# Revit family: 33-76-001 DN80-400
name_source: partatom
category: Pipe Accessories
units: mm (PartAtom-declared; Revit-internal decimal feet)

## family parameters
Always vertical = No
Cut with Voids When Loaded = No
Part Type = Valve - Breaks Into
Round Connector Dimension = Use Diameter
Shared = No
Work Plane-Based = No

## types (8) — shared parameters
1 = 1 mm  [stored 0.00328084 ft]
2 = 2 mm  [stored 0.00656168 ft]
DN080_PN16 = 33-080-76-0140099
33-080-76-0140099
DN100_PN16 = 33-100-76-0140099
DN150_PN16 = 33-150-76-0140099
DN200_PN16 = 33-200-76-0140099
DN250_PN16 = 33-250-76-0140099
DN300_PN16 = 33-300-76-0140087
DN350_PN16 = 33-350-76-0140087
DN400_PN16 = 33-400-76-0140087
Description_ = AVK GATE VALVE, SOCKET ENDS, PN16
Search_table = 33-76-001 DN80-400
T1 = 16 mm  [stored 0.0524934 ft]
Thickness = 9 mm  [stored 0.0295276 ft]
URL product pages = https://www.avkvalves.com
zero-valued in all types: Bonnet_FL_T, Default Elevation, Dim4

## per-type parameters (varying)
- DN080_PN16: Body_H=210 mm; Body_dim1=78 mm; Body_dim2=45 mm; Bolt=15 mm  [stored 0.0492126 ft]; Bolt_T=9 mm  [stored 0.0295276 ft]; Bonne_end=338 mm; Bonnet_Bolt1=9 mm  [stored 0.0295276 ft]; Bonnet_Bolt2=14 mm  [stored 0.0459318 ft]; Bonnet_W=72 mm; Bonnet_dim=43 mm; Bonnet_dim1=58 mm; Bonnet_dim2=8 mm  [stored 0.0262467 ft]; Bonnet_dim3=43 mm; Bonnet_dim4=35 mm; Bonnet_dim5=28 mm  [stored 0.0918635 ft]; Bonnet_dim6=25 mm  [stored 0.082021 ft]; Bore=40 mm  [stored 0.131234 ft]; DN=80 mm; Dd=101 mm; Dim1=67 mm; Dim2=75 mm; Dim3=66 mm; Disk=47 mm  [stored 0.154199 ft]; EPDM=99 mm; F1=17 mm  [stored 0.0557743 ft]; Fillet=15 mm  [stored 0.0492126 ft]; H=84 mm; H3=375 mm; L=298 mm; Location1=262 mm; Location2=75 mm; Rib_dim1=38 mm; Rib_dim2=31 mm; W=173 mm; W_actual=87 mm
- DN100_PN16: Body_H=235 mm; Body_dim1=87 mm; Body_dim2=48 mm; Bolt=17 mm  [stored 0.0557743 ft]; Bolt_T=10 mm  [stored 0.0328084 ft]; Bonne_end=367 mm; Bonnet_Bolt1=11 mm  [stored 0.0360892 ft]; Bonnet_Bolt2=16 mm  [stored 0.0524934 ft]; Bonnet_W=81 mm; Bonnet_dim=48 mm; Bonnet_dim1=62 mm; Bonnet_dim2=9 mm  [stored 0.0295276 ft]; Bonnet_dim3=48 mm; Bonnet_dim4=37 mm; Bonnet_dim5=30 mm  [stored 0.0984252 ft]; Bonnet_dim6=27 mm  [stored 0.0885827 ft]; Bore=50 mm; DN=100 mm; Dd=121 mm; Dim1=75 mm; Dim2=84 mm; Dim3=75 mm; Disk=50 mm; EPDM=119 mm; F1=19 mm  [stored 0.062336 ft]; Fillet=18 mm  [stored 0.0590551 ft]; H=94 mm; H3=408 mm; L=317 mm; Location1=279 mm; Location2=79 mm; Rib_dim1=43 mm; Rib_dim2=34 mm; W=194 mm; W_actual=97 mm
- DN150_PN16: Body_H=303 mm; Body_dim1=123 mm; Body_dim2=53 mm; Bolt=17 mm  [stored 0.0557743 ft]; Bolt_T=10 mm  [stored 0.0328084 ft]; Bonne_end=477 mm; Bonnet_Bolt1=12 mm  [stored 0.0393701 ft]; Bonnet_Bolt2=18 mm  [stored 0.0590551 ft]; Bonnet_W=114 mm; Bonnet_dim=48 mm; Bonnet_dim1=68 mm; Bonnet_dim2=10 mm  [stored 0.0328084 ft]; Bonnet_dim3=48 mm; Bonnet_dim4=41 mm; Bonnet_dim5=33 mm; Bonnet_dim6=30 mm  [stored 0.0984252 ft]; Bore=75 mm; DN=150 mm; Dd=173 mm; Dim1=97 mm; Dim2=110 mm; Dim3=100 mm; Disk=55 mm; EPDM=171 mm; F1=19 mm  [stored 0.062336 ft]; Fillet=20 mm  [stored 0.0656168 ft]; H=121 mm; H3=530 mm; L=351 mm; Location1=309 mm; Location2=88 mm; Rib_dim1=61 mm; Rib_dim2=49 mm; W=274 mm; W_actual=137 mm
- DN200_PN16: Body_H=368 mm; Body_dim1=150 mm; Body_dim2=58 mm; Bolt=22 mm  [stored 0.0721785 ft]; Bolt_T=12 mm  [stored 0.0393701 ft]; Bonne_end=581 mm; Bonnet_Bolt1=13 mm  [stored 0.0426509 ft]; Bonnet_Bolt2=20 mm  [stored 0.0656168 ft]; Bonnet_W=139 mm; Bonnet_dim=60 mm; Bonnet_dim1=75 mm; Bonnet_dim2=11 mm  [stored 0.0360892 ft]; Bonnet_dim3=60 mm; Bonnet_dim4=45 mm; Bonnet_dim5=36 mm; Bonnet_dim6=33 mm; Bore=100 mm; DN=200 mm; Dd=225 mm; Dim1=110 mm; Dim2=140 mm; Dim3=125 mm; Disk=60 mm; EPDM=223 mm; F1=24 mm  [stored 0.0787402 ft]; Fillet=22 mm  [stored 0.0721785 ft]; H=147 mm; H3=646 mm; L=387 mm; Location1=341 mm; Location2=97 mm; Rib_dim1=74 mm; Rib_dim2=59 mm; W=334 mm; W_actual=167 mm
- DN250_PN16: Body_H=438 mm; Body_dim1=190 mm; Body_dim2=70 mm; Bolt=24 mm  [stored 0.0787402 ft]; Bolt_T=14 mm  [stored 0.0459318 ft]; Bonne_end=729 mm; Bonnet_Bolt1=14 mm  [stored 0.0459318 ft]; Bonnet_Bolt2=22 mm  [stored 0.0721785 ft]; Bonnet_W=175 mm; Bonnet_dim=68 mm; Bonnet_dim1=91 mm; Bonnet_dim2=12 mm  [stored 0.0393701 ft]; Bonnet_dim3=68 mm; Bonnet_dim4=55 mm; Bonnet_dim5=44 mm; Bonnet_dim6=39 mm  [stored 0.127953 ft]; Bore=125 mm; DN=250 mm; Dd=277 mm; Dim1=115 mm; Dim2=165 mm; Dim3=150 mm; Disk=72 mm; EPDM=275 mm; F1=27 mm  [stored 0.0885827 ft]; Fillet=24 mm  [stored 0.0787402 ft]; H=175 mm; H3=810 mm; L=428 mm; Location1=377 mm; Location2=107 mm; Rib_dim1=94 mm; Rib_dim2=75 mm; W=422 mm; W_actual=211 mm
- DN300_PN16: Body_H=525 mm; Body_dim1=203 mm; Body_dim2=69 mm; Bolt=24 mm  [stored 0.0787402 ft]; Bolt_T=14 mm  [stored 0.0459318 ft]; Bonne_end=829 mm; Bonnet_Bolt1=16 mm  [stored 0.0524934 ft]; Bonnet_Bolt2=23 mm; Bonnet_W=188 mm; Bonnet_dim=68 mm; Bonnet_dim1=89 mm; Bonnet_dim2=13 mm  [stored 0.0426509 ft]; Bonnet_dim3=68 mm; Bonnet_dim4=54 mm; Bonnet_dim5=43 mm; Bonnet_dim6=39 mm  [stored 0.127953 ft]; Bore=150 mm; DN=300 mm; Dd=329 mm; Dim1=130 mm; Dim2=195 mm; Dim3=182 mm; Disk=71 mm; EPDM=327 mm; F1=27 mm  [stored 0.0885827 ft]; Fillet=26 mm; H=210 mm; H3=921 mm; L=458 mm; Location1=403 mm; Location2=115 mm; Rib_dim1=100 mm; Rib_dim2=80 mm; W=452 mm; W_actual=226 mm
- DN350_PN16: Body_H=570 mm; Body_dim1=254 mm; Body_dim2=78 mm; Bolt=29 mm; Bolt_T=16 mm  [stored 0.0524934 ft]; Bonne_end=1037 mm; Bonnet_Bolt1=17 mm  [stored 0.0557743 ft]; Bonnet_Bolt2=25 mm  [stored 0.082021 ft]; Bonnet_W=234 mm; Bonnet_dim=185 mm; Bonnet_dim1=101 mm; Bonnet_dim2=14 mm  [stored 0.0459318 ft]; Bonnet_dim3=80 mm; Bonnet_dim4=61 mm; Bonnet_dim5=49 mm; Bonnet_dim6=44 mm; Bore=175 mm; DN=350 mm; Dd=381 mm; Dim1=108 mm; Dim2=215 mm; Dim3=205 mm; Disk=80 mm; EPDM=379 mm; F1=32 mm  [stored 0.104987 ft]; Fillet=28 mm  [stored 0.0918635 ft]; H=228 mm; H3=1152 mm; L=460 mm; Location1=405 mm; Location2=115 mm; Rib_dim1=125 mm; Rib_dim2=100 mm; W=564 mm; W_actual=282 mm
- DN400_PN16: Body_H=638 mm; Body_dim1=254 mm; Body_dim2=80 mm; Bolt=29 mm; Bolt_T=16 mm  [stored 0.0524934 ft]; Bonne_end=1088 mm; Bonnet_Bolt1=18 mm  [stored 0.0590551 ft]; Bonnet_Bolt2=27 mm  [stored 0.0885827 ft]; Bonnet_W=234 mm; Bonnet_dim=165 mm; Bonnet_dim1=104 mm; Bonnet_dim2=15 mm  [stored 0.0492126 ft]; Bonnet_dim3=80 mm; Bonnet_dim4=62 mm; Bonnet_dim5=50 mm; Bonnet_dim6=45 mm; Bore=200 mm; DN=400 mm; Dd=432 mm; Dim1=110 mm; Dim2=240 mm; Dim3=230 mm; Disk=82 mm; EPDM=430 mm; F1=32 mm  [stored 0.104987 ft]; Fillet=30 mm  [stored 0.0984252 ft]; H=255 mm; H3=1209 mm; L=460 mm; Location1=405 mm; Location2=115 mm; Rib_dim1=125 mm; Rib_dim2=100 mm; W=564 mm; W_actual=282 mm

note: [stored X ft] marks values corroborated as IEEE doubles in the binary element streams (Revit-internal decimal feet)

## geometry (parser evidence)
native form markers: Sweep x7
no freeform markers — native parametric forms only
